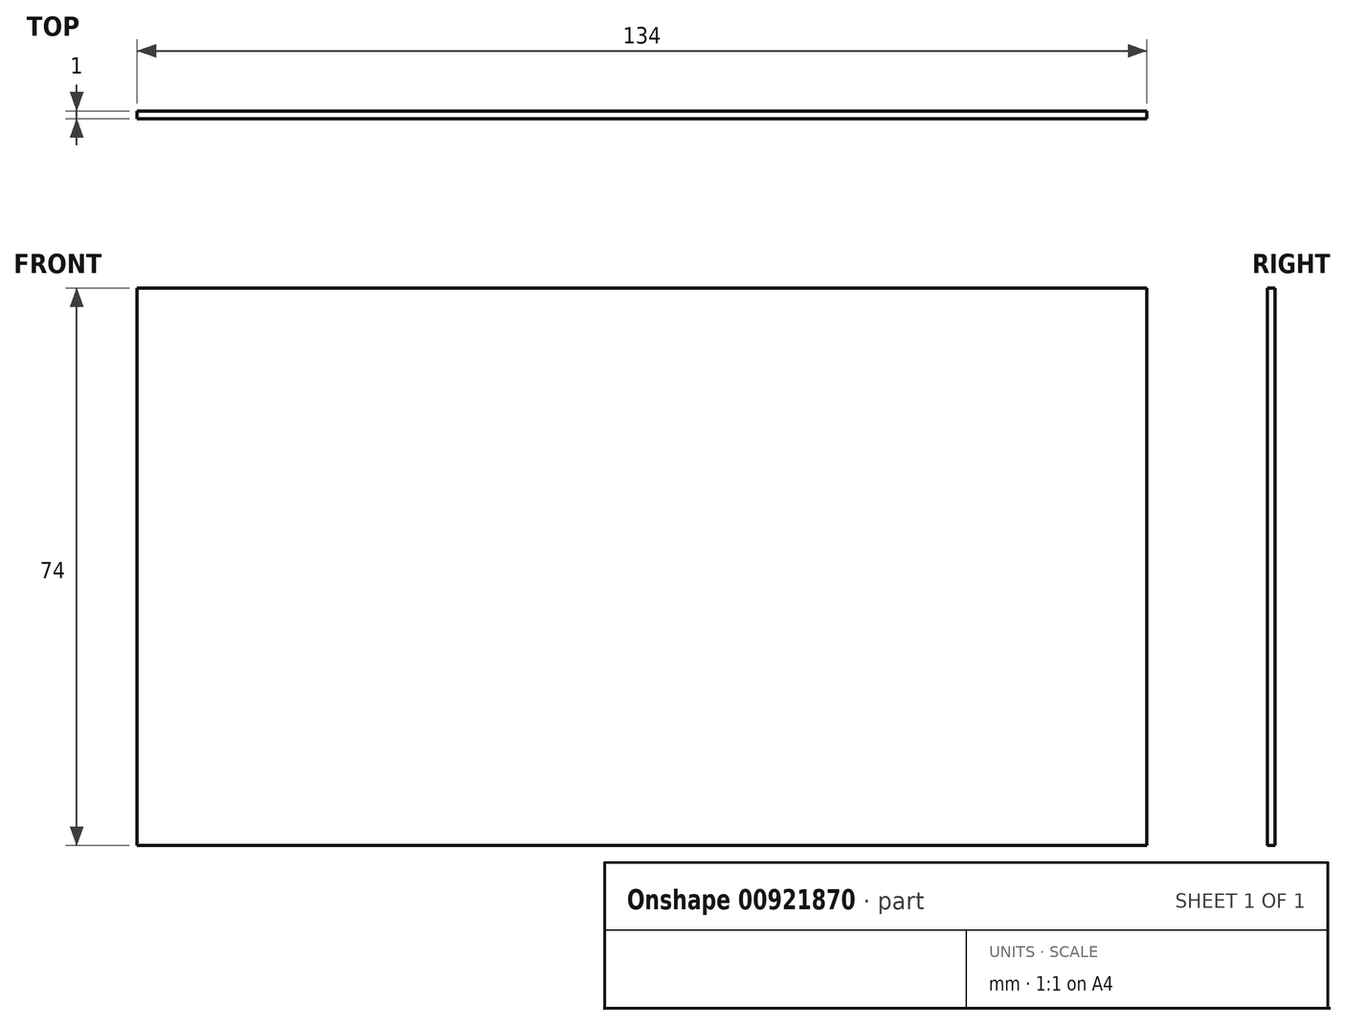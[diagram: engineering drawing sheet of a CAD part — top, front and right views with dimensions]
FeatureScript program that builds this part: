
annotation { "Feature Type Name" : "Feature", "Feature Type Description" : "" }
export const myFeature = defineFeature(function(context is Context, id is Id, definition is map)
    precondition{}
    {
        {
            var Q0;
            Q0=qCreatedBy(makeId("Front.planeOp"),FACE);
            var sketch = newSketch(context, id + "F0", { "sketchPlane" : qUnion([Q0])});
            skLineSegment(sketch, "E0.bottom", {"start": v(67, -37) * mm, "end": v(-67, -37) * mm});
            skLineSegment(sketch, "E0.top", {"start": v(67, 37) * mm, "end": v(-67, 37) * mm});
            skLineSegment(sketch, "E0.left", {"start": v(67, -37) * mm, "end": v(67, 37) * mm});
            skLineSegment(sketch, "E0.right", {"start": v(-67, -37) * mm, "end": v(-67, 37) * mm});
            skPoint(sketch, "E0.middle", {"position": v(0, 0) * mm});
            skSolve(sketch);
        }
        {
            var Q0;
            Q0=makeQuery(id+"F0.imprint","IMPRINT",FACE,{"disambiguationData":[TD([[makeQuery(id+"F0.imprint","IMPRINT",EDGE,{"derivedFrom":sQuery(id+"F0.wireOp",EDGE,"E0.bottom")}),-1.0]])]});
            extrude(context, id + "F1", {"entities" : qUnion([Q0]), "depth" : 1 * mm, "offsetDistance" : 25 * mm});
        }
    });
